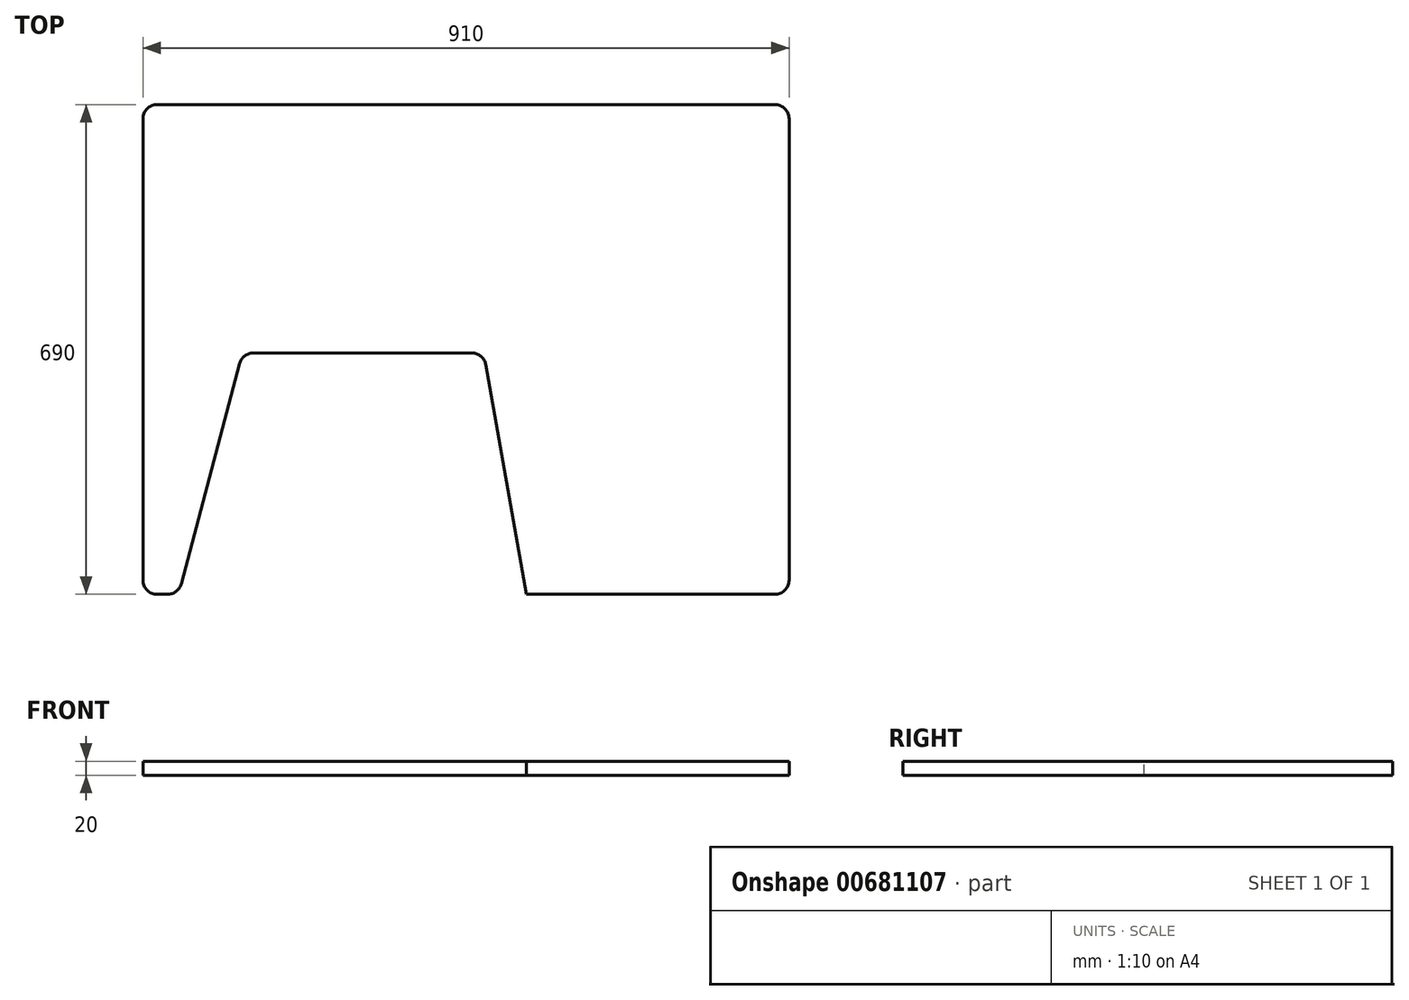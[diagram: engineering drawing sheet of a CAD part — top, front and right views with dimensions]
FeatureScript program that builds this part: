
annotation { "Feature Type Name" : "Feature", "Feature Type Description" : "" }
export const myFeature = defineFeature(function(context is Context, id is Id, definition is map)
    precondition{}
    {
        {
            var Q0;
            Q0=qCreatedBy(makeId("Top.planeOp"),FACE);
            var sketch = newSketch(context, id + "F0", { "sketchPlane" : qUnion([Q0])});
            skLineSegment(sketch, "E0.bottom", {"start": v(455, -345) * mm, "end": v(-455, -345) * mm});
            skLineSegment(sketch, "E0.top", {"start": v(455, 345) * mm, "end": v(-455, 345) * mm});
            skLineSegment(sketch, "E0.left", {"start": v(455, -345) * mm, "end": v(455, 345) * mm});
            skLineSegment(sketch, "E0.right", {"start": v(-455, -345) * mm, "end": v(-455, 345) * mm});
            skPoint(sketch, "E0.middle", {"position": v(0, 0) * mm});
            skSolve(sketch);
        }
        {
            var Q0;
            Q0=makeQuery(id+"F0.imprint","IMPRINT",FACE,{"disambiguationData":[TD([[makeQuery(id+"F0.imprint","IMPRINT",EDGE,{"derivedFrom":sQuery(id+"F0.wireOp",EDGE,"E0.bottom")}),-1.0]])]});
            extrude(context, id + "F1", {"entities" : qUnion([Q0]), "depth" : 20 * mm});
        }
        {
            var Q0;
            Q0=makeQuery(id+"F1.opExtrude","CAP_FACE",FACE,{"disambiguationData":[OSD([sQuery(id+"F0.wireOp",EDGE,"E0.bottom"),sQuery(id+"F0.wireOp",EDGE,"E0.top"),sQuery(id+"F0.wireOp",EDGE,"E0.left"),sQuery(id+"F0.wireOp",EDGE,"E0.right")])],"isStart":false});
            var sketch = newSketch(context, id + "F2", { "sketchPlane" : qUnion([Q0])});
            skLineSegment(sketch, "E1.bottom", {"start": v(-315, -345) * mm, "end": v(25, -345) * mm});
            skLineSegment(sketch, "E1.top", {"start": v(-315, -5) * mm, "end": v(25, -5) * mm});
            skLineSegment(sketch, "E1.left", {"start": v(-315, -345) * mm, "end": v(-315, -5) * mm});
            skLineSegment(sketch, "E1.right", {"start": v(25, -345) * mm, "end": v(25, -5) * mm});
            skLineSegment(sketch, "E2", {"start": v(-315, -5) * mm, "end": v(-405, -345) * mm});
            skLineSegment(sketch, "E3", {"start": v(25, -5) * mm, "end": v(85, -345) * mm});
            skSolve(sketch);
        }
        {
            var Q0;
            Q0=makeQuery(id+"F2.imprint","IMPRINT",FACE,{"disambiguationData":[TD([[makeQuery(id+"F2.imprint","IMPRINT",EDGE,{"derivedFrom":sQuery(id+"F2.wireOp",EDGE,"E1.bottom")}),-1.0]])]});
            var Q1;
            {var subQ0=sQuery(id+"F2.wireOp",EDGE,"E1.left");Q1=makeQuery(id+"F2.imprint","IMPRINT",FACE,{"disambiguationData":[TD([[makeQuery(id+"F2.imprint","IMPRINT",EDGE,{"derivedFrom":subQ0}),1.0]])]});}
            var Q2;
            {var subQ0=sQuery(id+"F2.wireOp",EDGE,"E1.right");Q2=makeQuery(id+"F2.imprint","IMPRINT",FACE,{"disambiguationData":[TD([[makeQuery(id+"F2.imprint","IMPRINT",EDGE,{"derivedFrom":subQ0}),-1.0]])]});}
            extrude(context, id + "F3", {"entities" : qUnion([Q0, Q1, Q2]), "operationType" : NewBodyOperationType.REMOVE, "oppositeDirection" : true, "depth" : 25 * mm, "offsetDistance" : 25 * mm});
        }
        {
            var Q0;
            Q0=makeQuery(id+"F3.boolean.opBoolean","COPY",EDGE,{"derivedFrom":makeQuery(id+"F3.opExtrude","SWEPT_EDGE",EDGE,{"disambiguationData":[OSD([sQuery(id+"F2.wireOp",EDGE,"E1.top"),sQuery(id+"F2.wireOp",EDGE,"E1.left")])]})});
            var Q1;
            Q1=makeQuery(id+"F3.boolean.opBoolean","COPY",EDGE,{"derivedFrom":makeQuery(id+"F3.opExtrude","SWEPT_EDGE",EDGE,{"disambiguationData":[OSD([sQuery(id+"F2.wireOp",EDGE,"E1.top"),sQuery(id+"F2.wireOp",EDGE,"E1.right")])]})});
            var Q2;
            Q2=makeQuery(id+"F3.boolean.opBoolean","COPY",EDGE,{"derivedFrom":makeQuery(id+"F3.opExtrude","SWEPT_EDGE",EDGE,{"disambiguationData":[OSD([sQuery(id+"F0.wireOp",EDGE,"E0.bottom"),sQuery(id+"F2.wireOp",EDGE,"E1.bottom"),sQuery(id+"F2.wireOp",EDGE,"E1.right")])]})});
            var Q3;
            Q3=makeQuery(id+"F3.boolean.opBoolean","COPY",EDGE,{"derivedFrom":makeQuery(id+"F3.opExtrude","SWEPT_EDGE",EDGE,{"disambiguationData":[OSD([sQuery(id+"F0.wireOp",EDGE,"E0.bottom"),sQuery(id+"F2.wireOp",EDGE,"E1.bottom"),sQuery(id+"F2.wireOp",EDGE,"E1.left")])]})});
            var Q4;
            Q4=makeQuery(id+"F1.opExtrude","SWEPT_EDGE",EDGE,{"disambiguationData":[OSD([sQuery(id+"F0.wireOp",EDGE,"E0.bottom"),sQuery(id+"F0.wireOp",EDGE,"E0.left")])]});
            var Q5;
            Q5=makeQuery(id+"F1.opExtrude","SWEPT_EDGE",EDGE,{"disambiguationData":[OSD([sQuery(id+"F0.wireOp",EDGE,"E0.top"),sQuery(id+"F0.wireOp",EDGE,"E0.left")])]});
            var Q6;
            Q6=makeQuery(id+"F1.opExtrude","SWEPT_EDGE",EDGE,{"disambiguationData":[OSD([sQuery(id+"F0.wireOp",EDGE,"E0.top"),sQuery(id+"F0.wireOp",EDGE,"E0.right")])]});
            var Q7;
            Q7=makeQuery(id+"F1.opExtrude","SWEPT_EDGE",EDGE,{"disambiguationData":[OSD([sQuery(id+"F0.wireOp",EDGE,"E0.bottom"),sQuery(id+"F0.wireOp",EDGE,"E0.right")])]});
            fillet(context, id + "F4", {"entities" : qUnion([Q0, Q1, Q2, Q3, Q4, Q5, Q6, Q7]), "radius" : 20 * mm, "tangentPropagation" : true, "allowEdgeOverflow" : false});
        }
    });
